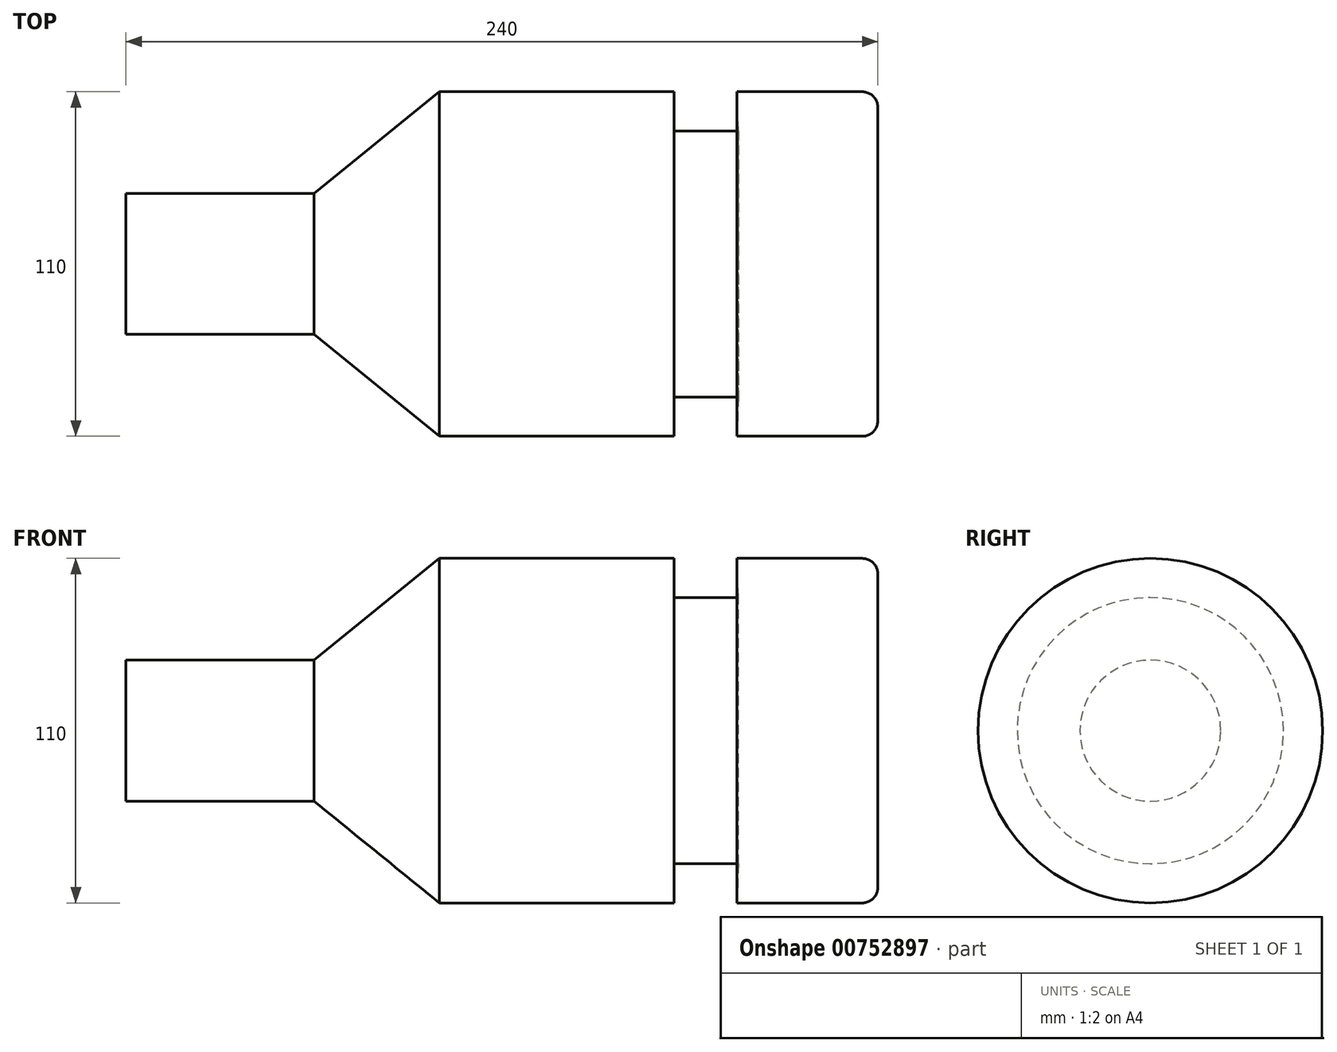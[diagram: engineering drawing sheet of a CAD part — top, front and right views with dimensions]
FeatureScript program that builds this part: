
annotation { "Feature Type Name" : "Feature", "Feature Type Description" : "" }
export const myFeature = defineFeature(function(context is Context, id is Id, definition is map)
    precondition{}
    {
        {
            var Q0;
            Q0=qCreatedBy(makeId("Front.planeOp"),FACE);
            var sketch = newSketch(context, id + "F0", { "sketchPlane" : qUnion([Q0])});
            skLineSegment(sketch, "E0", {"start": v(0, 0) * mm, "end": v(0, 22.5) * mm});
            skLineSegment(sketch, "E1", {"start": v(0, 22.5) * mm, "end": v(60, 22.5) * mm});
            skLineSegment(sketch, "E2", {"start": v(60, 22.5) * mm, "end": v(100, 55) * mm});
            skLineSegment(sketch, "E3", {"start": v(100, 55) * mm, "end": v(175, 55) * mm});
            skLineSegment(sketch, "E4", {"start": v(195, 55) * mm, "end": v(240, 55) * mm});
            skLineSegment(sketch, "E5", {"start": v(240, 55) * mm, "end": v(240, 0) * mm});
            skLineSegment(sketch, "E6", {"start": v(240, 0) * mm, "end": v(0, 0) * mm});
            skLineSegment(sketch, "E7", {"start": v(0, 0) * mm, "end": v(-96.57, 0) * mm, "construction": true});
            skLineSegment(sketch, "E8", {"start": v(175, 55) * mm, "end": v(175, 42.5) * mm});
            skLineSegment(sketch, "E9", {"start": v(175, 42.5) * mm, "end": v(195.52, 42.5) * mm});
            skLineSegment(sketch, "E10", {"start": v(195.52, 42.5) * mm, "end": v(195, 55) * mm});
            skSolve(sketch);
        }
        {
            var Q0;
            Q0=makeQuery(id+"F0.imprint","IMPRINT",FACE,{"disambiguationData":[TD([[makeQuery(id+"F0.imprint","IMPRINT",EDGE,{"derivedFrom":sQuery(id+"F0.wireOp",EDGE,"E0")}),-1.0]])]});
            var Q1;
            Q1=sQuery(id+"F0.wireOp",EDGE,"E7");
            revolve(context, id + "F1", {"surfaceOperationType" : NewSurfaceOperationType.NEW, "entities" : qUnion([Q0]), "axis" : qUnion([Q1]), "revolveType" : RevolveType.FULL});
        }
        {
            var Q0;
            Q0=makeQuery(id+"F1.opRevolve","SWEPT_EDGE",EDGE,{"disambiguationData":[OSD([sQuery(id+"F0.wireOp",EDGE,"E4"),sQuery(id+"F0.wireOp",EDGE,"E5")])]});
            fillet(context, id + "F2", {"entities" : qUnion([Q0]), "radius" : 5 * mm, "tangentPropagation" : true, "allowEdgeOverflow" : false});
        }
    });
